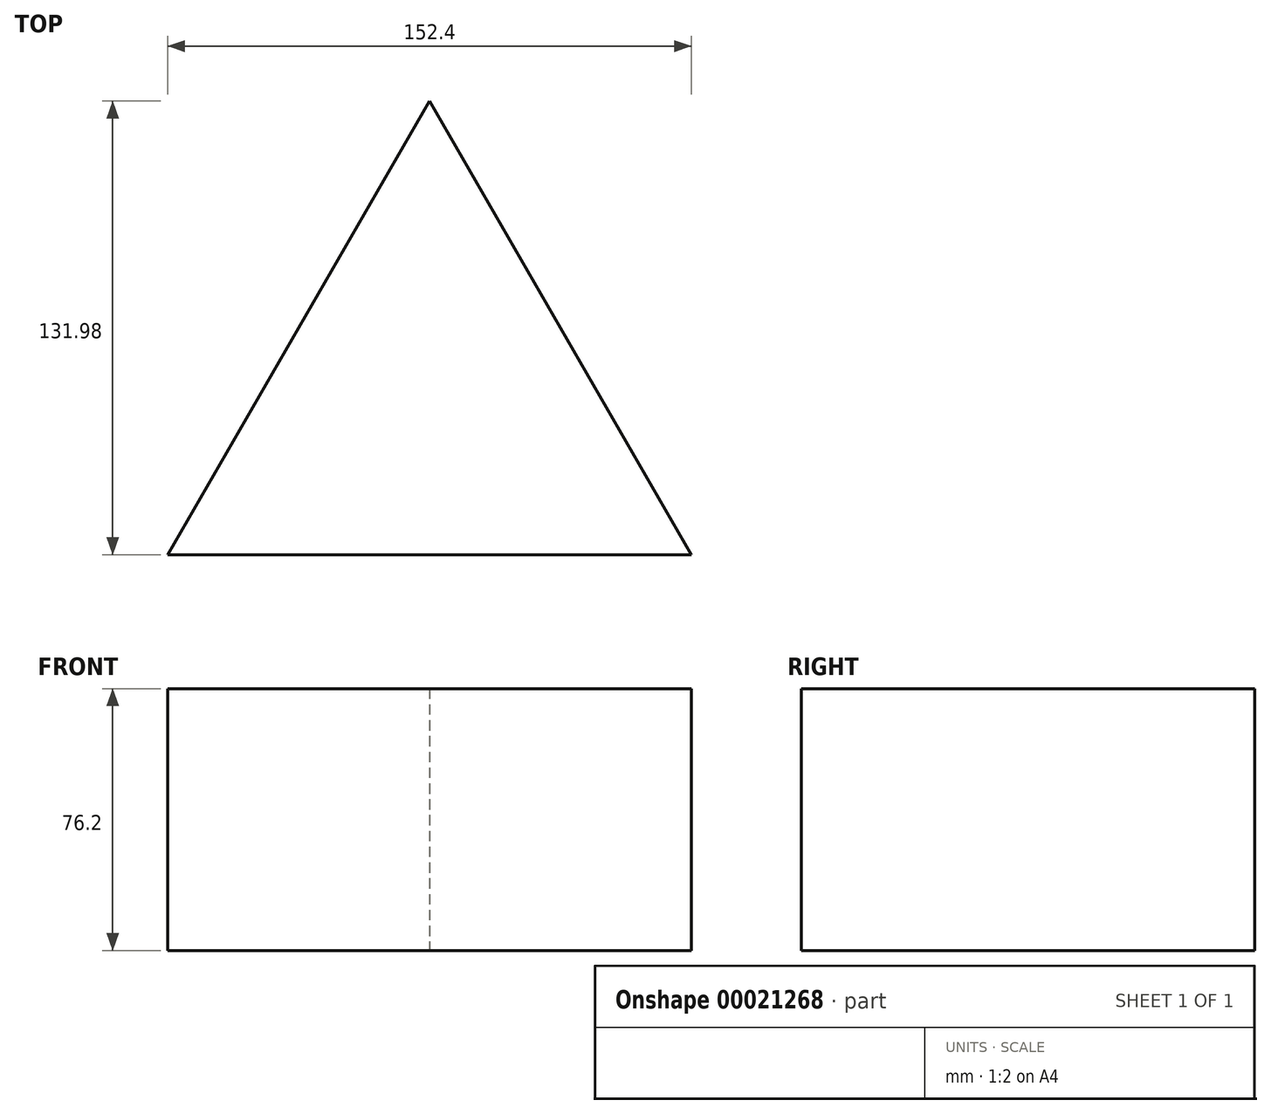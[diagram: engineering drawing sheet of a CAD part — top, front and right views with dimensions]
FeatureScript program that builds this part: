
annotation { "Feature Type Name" : "Feature", "Feature Type Description" : "" }
export const myFeature = defineFeature(function(context is Context, id is Id, definition is map)
    precondition{}
    {
        {
            var Q0;
            Q0=qCreatedBy(makeId("Top.planeOp"),FACE);
            var sketch = newSketch(context, id + "F0", { "sketchPlane" : qUnion([Q0])});
            skLineSegment(sketch, "E0", {"start": v(0, 68.1) * mm, "end": v(-76.2, -63.88) * mm});
            skLineSegment(sketch, "E1", {"start": v(-76.2, -63.88) * mm, "end": v(76.2, -63.88) * mm});
            skLineSegment(sketch, "E2", {"start": v(76.2, -63.88) * mm, "end": v(0, 68.1) * mm});
            skLineSegment(sketch, "E3", {"start": v(0, 68.1) * mm, "end": v(0, -63.88) * mm});
            skLineSegment(sketch, "E4", {"start": v(0, -63.88) * mm, "end": v(0, 68.1) * mm});
            skLineSegment(sketch, "E5", {"start": v(76.2, -63.88) * mm, "end": v(-38.1, 2.1) * mm});
            skLineSegment(sketch, "E6", {"start": v(-38.1, 2.1) * mm, "end": v(76.2, -63.88) * mm});
            skLineSegment(sketch, "E7", {"start": v(-76.2, -63.88) * mm, "end": v(38.1, 2.1) * mm});
            skLineSegment(sketch, "E8", {"start": v(38.1, 2.1) * mm, "end": v(-76.2, -63.88) * mm});
            skSolve(sketch);
        }
        {
            var Q0;
            {var subQ1=sQuery(id+"F0.wireOp",EDGE,"E6");var subQ3=sQuery(id+"F0.wireOp",EDGE,"E0");var subQ5=makeQuery(id+"F0.imprint","INTERSECT",VERTEX,{"derivedFrom":[subQ3,subQ1]});Q0=makeQuery(id+"F0.imprint","IMPRINT",FACE,{"disambiguationData":[TD([[makeQuery(id+"F0.imprint","IMPRINT",EDGE,{"disambiguationData":[TD([[subQ5,-1.0]])],"derivedFrom":subQ3}),1.0]])]});}
            var Q1;
            {var subQ1=sQuery(id+"F0.wireOp",EDGE,"E4");var subQ3=sQuery(id+"F0.wireOp",EDGE,"E1");var subQ5=makeQuery(id+"F0.imprint","INTERSECT",VERTEX,{"derivedFrom":[subQ3,subQ1]});Q1=makeQuery(id+"F0.imprint","IMPRINT",FACE,{"disambiguationData":[TD([[makeQuery(id+"F0.imprint","IMPRINT",EDGE,{"disambiguationData":[TD([[subQ5,1.0]])],"derivedFrom":subQ3}),1.0]])]});}
            var Q2;
            {var subQ1=sQuery(id+"F0.wireOp",EDGE,"E4");var subQ3=sQuery(id+"F0.wireOp",EDGE,"E1");var subQ5=makeQuery(id+"F0.imprint","INTERSECT",VERTEX,{"derivedFrom":[subQ3,subQ1]});Q2=makeQuery(id+"F0.imprint","IMPRINT",FACE,{"disambiguationData":[TD([[makeQuery(id+"F0.imprint","IMPRINT",EDGE,{"disambiguationData":[TD([[subQ5,-1.0]])],"derivedFrom":subQ3}),1.0]])]});}
            var Q3;
            {var subQ0=sQuery(id+"F0.wireOp",EDGE,"E8");var subQ3=sQuery(id+"F0.wireOp",EDGE,"E2");var subQ4=makeQuery(id+"F0.imprint","INTERSECT",VERTEX,{"derivedFrom":[subQ3,subQ0]});Q3=makeQuery(id+"F0.imprint","IMPRINT",FACE,{"disambiguationData":[TD([[makeQuery(id+"F0.imprint","IMPRINT",EDGE,{"disambiguationData":[TD([[subQ4,1.0]])],"derivedFrom":subQ3}),1.0]])]});}
            var Q4;
            {var subQ0=sQuery(id+"F0.wireOp",EDGE,"E8");var subQ3=sQuery(id+"F0.wireOp",EDGE,"E2");var subQ4=makeQuery(id+"F0.imprint","INTERSECT",VERTEX,{"derivedFrom":[subQ3,subQ0]});Q4=makeQuery(id+"F0.imprint","IMPRINT",FACE,{"disambiguationData":[TD([[makeQuery(id+"F0.imprint","IMPRINT",EDGE,{"disambiguationData":[TD([[subQ4,-1.0]])],"derivedFrom":subQ3}),1.0]])]});}
            var Q5;
            {var subQ0=sQuery(id+"F0.wireOp",EDGE,"E6");var subQ3=sQuery(id+"F0.wireOp",EDGE,"E0");var subQ4=makeQuery(id+"F0.imprint","INTERSECT",VERTEX,{"derivedFrom":[subQ3,subQ0]});Q5=makeQuery(id+"F0.imprint","IMPRINT",FACE,{"disambiguationData":[TD([[makeQuery(id+"F0.imprint","IMPRINT",EDGE,{"disambiguationData":[TD([[subQ4,1.0]])],"derivedFrom":subQ3}),1.0]])]});}
            extrude(context, id + "F1", {"entities" : qUnion([Q0, Q1, Q2, Q3, Q4, Q5]), "depth" : 76.2 * mm});
        }
    });
